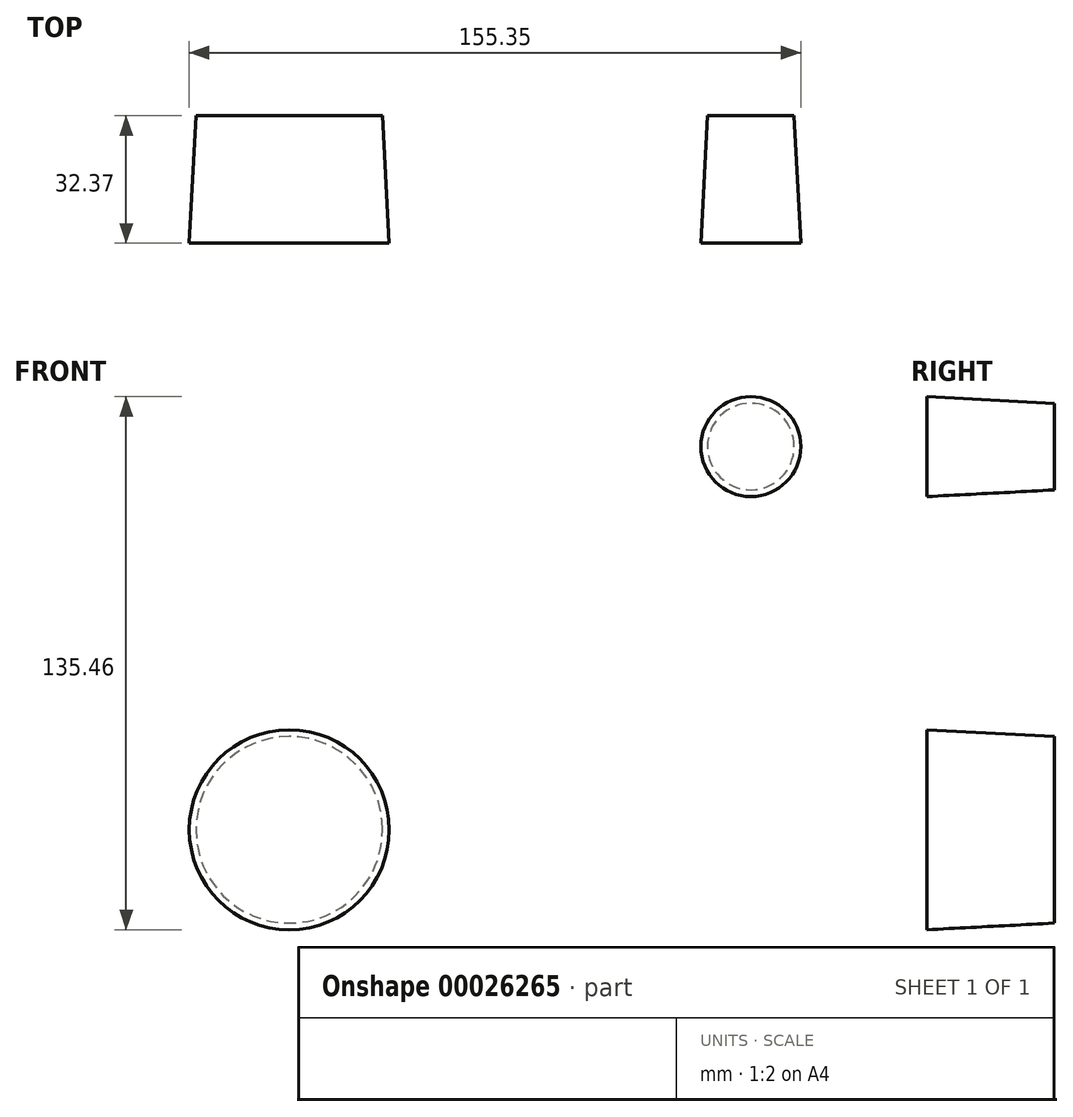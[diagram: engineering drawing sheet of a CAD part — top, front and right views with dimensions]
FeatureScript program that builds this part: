
annotation { "Feature Type Name" : "Feature", "Feature Type Description" : "" }
export const myFeature = defineFeature(function(context is Context, id is Id, definition is map)
    precondition{}
    {
        {
            var Q0;
            Q0=qCreatedBy(makeId("Front.planeOp"),FACE);
            var sketch = newSketch(context, id + "F0", { "sketchPlane" : qUnion([Q0])});
            skCircle(sketch, "E0", {"center": v(-162.57, -47.93) * mm, "radius": 44.45 * mm});
            skCircle(sketch, "E1", {"center": v(-162.57, -47.93) * mm, "radius": 25.4 * mm});
            skCircle(sketch, "E2", {"center": v(-45.32, 49.43) * mm, "radius": 25.4 * mm});
            skCircle(sketch, "E3", {"center": v(-45.32, 49.43) * mm, "radius": 12.7 * mm});
            skLineSegment(sketch, "E4", {"start": v(-173.66, -4.88) * mm, "end": v(-67.95, 60.95) * mm});
            skLineSegment(sketch, "E5", {"start": v(-123.88, -69.81) * mm, "end": v(-31.7, 27.99) * mm});
            skLineSegment(sketch, "E6", {"start": v(-162.57, -47.93) * mm, "end": v(-45.32, 49.43) * mm});
            skCircle(sketch, "E7", {"center": v(-352.5, 9.96) * mm, "radius": 25.4 * mm});
            skCircle(sketch, "E8", {"center": v(-352.5, 9.96) * mm, "radius": 12.7 * mm});
            skLineSegment(sketch, "E9", {"start": v(-343.36, 33.66) * mm, "end": v(-191.6, -14.28) * mm});
            skLineSegment(sketch, "E10", {"start": v(-363.4, -12.98) * mm, "end": v(-188.72, -83.87) * mm});
            skLineSegment(sketch, "E11", {"start": v(-352.5, 9.96) * mm, "end": v(-206.69, -34.36) * mm});
            skSolve(sketch);
        }
        {
            var Q0;
            Q0 = qSketchRegion(id + "F2", true);
            var Q1;
            Q1=makeQuery(id+"F0.imprint","IMPRINT",FACE,{"disambiguationData":[TD([[makeQuery(id+"F0.imprint","IMPRINT",EDGE,{"derivedFrom":sQuery(id+"F0.wireOp",EDGE,"E1")}),1.0]])]});
            var Q2;
            {var subQ5=sQuery(id+"F0.wireOp",EDGE,"E4");Q2=makeQuery(id+"F0.imprint","IMPRINT",FACE,{"disambiguationData":[TD([[makeQuery(id+"F0.imprint","IMPRINT",EDGE,{"derivedFrom":subQ5}),-1.0]])]});}
            var Q3;
            {var subQ5=sQuery(id+"F0.wireOp",EDGE,"E5");Q3=makeQuery(id+"F0.imprint","IMPRINT",FACE,{"disambiguationData":[TD([[makeQuery(id+"F0.imprint","IMPRINT",EDGE,{"derivedFrom":subQ5}),1.0]])]});}
            var Q4;
            Q4=makeQuery(id+"F0.imprint","IMPRINT",FACE,{"disambiguationData":[TD([[makeQuery(id+"F0.imprint","IMPRINT",EDGE,{"derivedFrom":sQuery(id+"F0.wireOp",EDGE,"E3")}),1.0]])]});
            var Q5;
            Q5=makeQuery(id+"F0.imprint","IMPRINT",FACE,{"disambiguationData":[TD([[makeQuery(id+"F0.imprint","IMPRINT",EDGE,{"derivedFrom":sQuery(id+"F0.wireOp",EDGE,"E8")}),1.0]])]});
            extrude(context, id + "F1", {"entities" : qUnion([Q0, Q1, Q2, Q3, Q4, Q5]), "oppositeDirection" : true, "depth" : 32.37 * mm, "hasDraft" : true, "draftAngle" : 3 * degree, "draftPullDirection" : true});
        }
        {
            var Q0;
            Q0=makeQuery(id+"F1.opExtrude","CAP_FACE",FACE,{"disambiguationData":[OSD([sQuery(id+"F0.wireOp",EDGE,"E0"),sQuery(id+"F0.wireOp",EDGE,"E1"),sQuery(id+"F0.wireOp",EDGE,"E2"),sQuery(id+"F0.wireOp",EDGE,"E3"),sQuery(id+"F0.wireOp",EDGE,"E4"),sQuery(id+"F0.wireOp",EDGE,"E5"),sQuery(id+"F0.wireOp",EDGE,"E7"),sQuery(id+"F0.wireOp",EDGE,"E8"),sQuery(id+"F0.wireOp",EDGE,"E9"),sQuery(id+"F0.wireOp",EDGE,"E10")])],"isStart":false});
            var sketch = newSketch(context, id + "F2", { "sketchPlane" : qUnion([Q0])});
            skArc(sketch, "E12", {"start": v(-350.98, -11.03) * mm, "mid": v(-337.57, -0.73) * mm, "end": v(-334.53, 15.9) * mm});
            skSolve(sketch);
        }
        {
            var Q0;
            Q0=makeQuery(id+"F1.opExtrude","SWEPT_BODY",BODY,{"disambiguationData":[OSD([sQuery(id+"F0.wireOp",EDGE,"E0"),sQuery(id+"F0.wireOp",EDGE,"E2"),sQuery(id+"F0.wireOp",EDGE,"E4"),sQuery(id+"F0.wireOp",EDGE,"E5")])]});
            deleteBodies(context, id + "F3", {"entities" : qUnion([Q0])});
        }
        {
            var Q0;
            Q0=makeQuery(id+"F1.opExtrude","SWEPT_BODY",BODY,{"disambiguationData":[OSD([sQuery(id+"F0.wireOp",EDGE,"E8")])]});
            deleteBodies(context, id + "F4", {"entities" : qUnion([Q0])});
        }
    });
